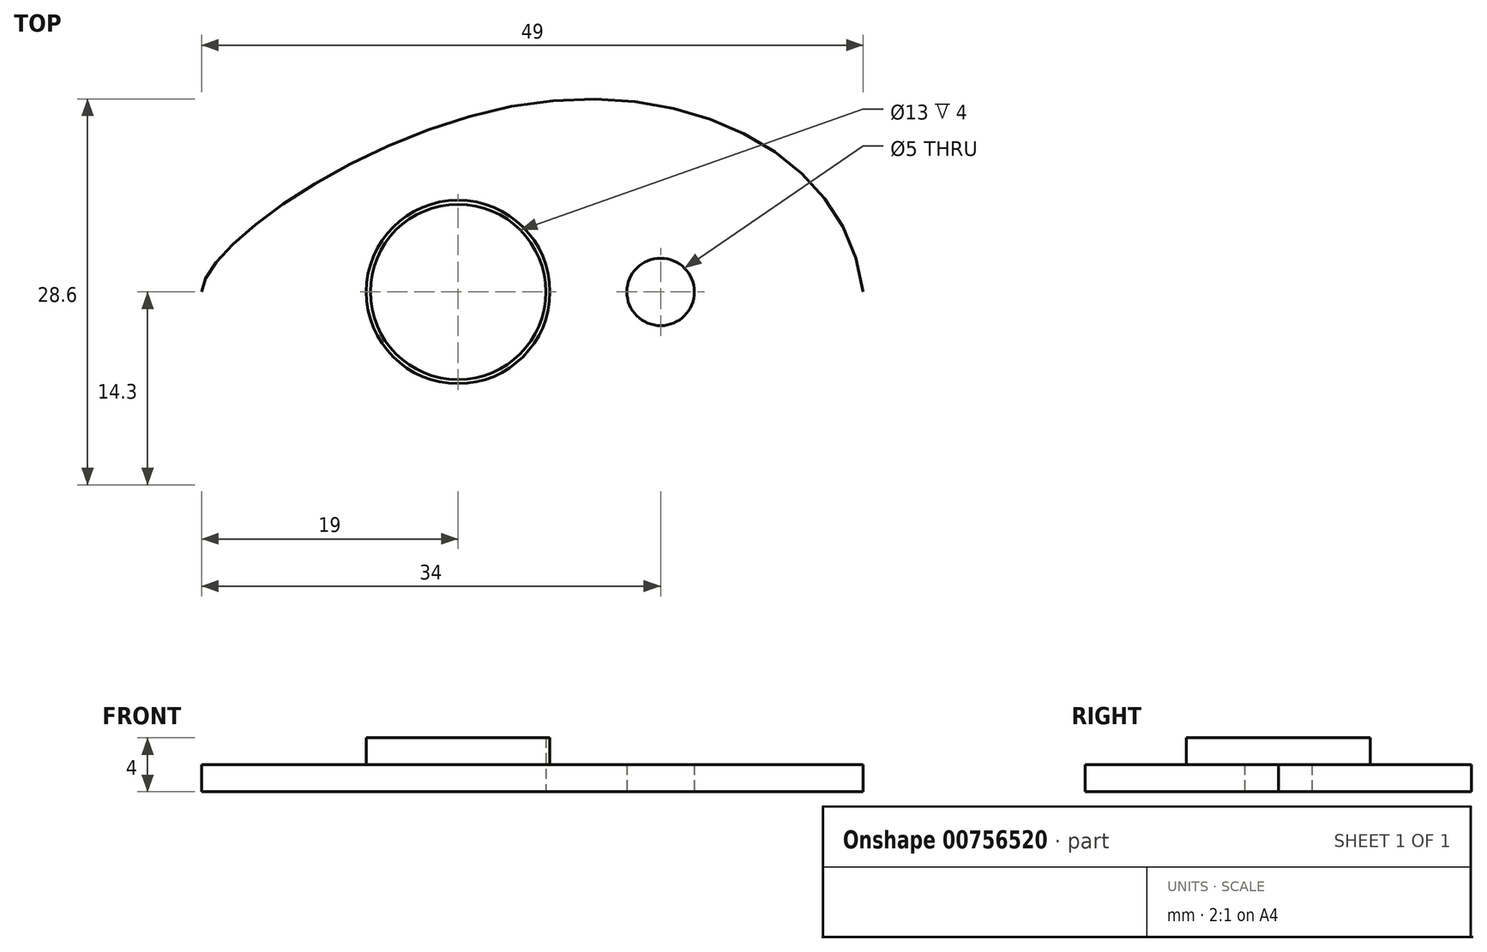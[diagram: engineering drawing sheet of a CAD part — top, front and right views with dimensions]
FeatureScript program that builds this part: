
annotation { "Feature Type Name" : "Feature", "Feature Type Description" : "" }
export const myFeature = defineFeature(function(context is Context, id is Id, definition is map)
    precondition{}
    {
        {
            var Q0;
            Q0=qCreatedBy(makeId("Top.planeOp"),FACE);
            var sketch = newSketch(context, id + "F0", { "sketchPlane" : qUnion([Q0])});
            skFitSpline(sketch, "E0", {"points": [v(-34, 0) * mm, v(-9.5, 14) * mm, v(15, 0) * mm], "startDerivative": vector(-0.01, 20.2) * mm, "endDerivative": vector(7.4, -60.56) * mm});
            skArc(sketch, "E1", {"start": v(-21.5, 0) * mm, "mid": v(-15, 6.5) * mm, "end": v(-8.5, 0) * mm});
            skPoint(sketch, "E1.startSnap0", {"position": v(-17, 0) * mm});
            skLineSegment(sketch, "E2", {"start": v(-34, 0) * mm, "end": v(-21.5, 0) * mm});
            skArc(sketch, "E3", {"start": v(-2.5, 0) * mm, "mid": v(0, 2.5) * mm, "end": v(2.5, 0) * mm});
            skLineSegment(sketch, "E4", {"start": v(-8.5, 0) * mm, "end": v(-2.5, 0) * mm});
            skLineSegment(sketch, "E5", {"start": v(2.5, 0) * mm, "end": v(15, 0) * mm});
            skSolve(sketch);
        }
        {
            var Q0;
            Q0=qSketchRegion(id+"F0",true);
            extrude(context, id + "F1", {"entities" : qUnion([Q0]), "depth" : 18 * mm, "offsetDistance" : 25 * mm});
        }
        {
            var Q0;
            Q0=makeQuery(id+"F1.opExtrude","SWEPT_BODY",BODY,{"disambiguationData":[OSD([sQuery(id+"F0.wireOp",EDGE,"E0"),sQuery(id+"F0.wireOp",EDGE,"E1"),sQuery(id+"F0.wireOp",EDGE,"McHGNHOU-62kw-HZgm-CWgZ-VDhnGf6BRuoS"),sQuery(id+"F0.wireOp",EDGE,"E2"),sQuery(id+"F0.wireOp",EDGE,"D958tiaN-heJL-5NL5-mns3-F5RS8ibdN3Pm"),sQuery(id+"F0.wireOp",EDGE,"xE7LKnkU-Hi0Y-gHIj-jbuS-JquG0hnZopf2")])]});
            var Q1;
            Q1=qCreatedBy(makeId("Front.planeOp"),FACE);
            mirror(context, id + "F2", {"operationType" : NewBodyOperationType.ADD, "entities" : qUnion([Q0]), "mirrorPlane" : qUnion([Q1])});
        }
        {
            var Q0;
            Q0=qCreatedBy(makeId("Top.planeOp"),FACE);
            var sketch = newSketch(context, id + "F3", { "sketchPlane" : qUnion([Q0])});
            skLineSegment(sketch, "E6", {"start": v(0, 0) * mm, "end": v(-15, 0) * mm});
            skCircle(sketch, "E7", {"center": v(-15, 0) * mm, "radius": 6.5 * mm});
            skCircle(sketch, "E8", {"center": v(-15, 0) * mm, "radius": 6.8 * mm});
            skSolve(sketch);
        }
        {
            var Q0;
            Q0=qSketchRegion(id+"F3",true);
            extrude(context, id + "F4", {"entities" : qUnion([Q0]), "operationType" : NewBodyOperationType.ADD, "depth" : 20 * mm, "offsetDistance" : 25 * mm});
        }
        {
            var Q0;
            Q0=qCreatedBy(makeId("Top.planeOp"),FACE);
            var sketch = newSketch(context, id + "F5", { "sketchPlane" : qUnion([Q0])});
            skCircle(sketch, "E9", {"center": v(0, 0) * mm, "radius": 4.75 * mm});
            skSolve(sketch);
        }
        {
            var Q0;
            Q0=qSketchRegion(id+"F5",true);
            extrude(context, id + "F6", {"entities" : qUnion([Q0]), "depth" : 15 * mm, "offsetDistance" : 25 * mm});
        }
        {
            var Q0;
            Q0=makeQuery(id+"F6.opExtrude","SWEPT_BODY",BODY,{"disambiguationData":[OSD([sQuery(id+"F5.wireOp",EDGE,"E9")])]});
            var Q1;
            Q1=makeQuery(id+"F1.opExtrude","SWEPT_BODY",BODY,{"disambiguationData":[OSD([sQuery(id+"F0.wireOp",EDGE,"E0"),sQuery(id+"F0.wireOp",EDGE,"E1"),sQuery(id+"F0.wireOp",EDGE,"McHGNHOU-62kw-HZgm-CWgZ-VDhnGf6BRuoS"),sQuery(id+"F0.wireOp",EDGE,"E2"),sQuery(id+"F0.wireOp",EDGE,"D958tiaN-heJL-5NL5-mns3-F5RS8ibdN3Pm"),sQuery(id+"F0.wireOp",EDGE,"xE7LKnkU-Hi0Y-gHIj-jbuS-JquG0hnZopf2")])]});
            booleanBodies(context, id + "F7", {"operationType" : BooleanOperationType.SUBTRACTION, "tools" : qUnion([Q0]), "targets" : qUnion([Q1])});
        }
        {
            var Q0;
            Q0=qCreatedBy(makeId("Top.planeOp"),FACE);
            var sketch = newSketch(context, id + "F8", { "sketchPlane" : qUnion([Q0])});
            skLineSegment(sketch, "E10.bottom", {"start": v(50, -30) * mm, "end": v(-50, -30) * mm});
            skLineSegment(sketch, "E10.top", {"start": v(50, 30) * mm, "end": v(-50, 30) * mm});
            skLineSegment(sketch, "E10.left", {"start": v(50, -30) * mm, "end": v(50, 30) * mm});
            skLineSegment(sketch, "E10.right", {"start": v(-50, -30) * mm, "end": v(-50, 30) * mm});
            skPoint(sketch, "E10.middle", {"position": v(0, 0) * mm});
            skSolve(sketch);
        }
        {
            var Q0;
            Q0=qSketchRegion(id+"F8",true);
            extrude(context, id + "F9", {"entities" : qUnion([Q0]), "depth" : 16 * mm, "offsetDistance" : 25 * mm});
        }
        {
            var Q0;
            Q0=makeQuery(id+"F9.opExtrude","SWEPT_BODY",BODY,{"disambiguationData":[OSD([sQuery(id+"F8.wireOp",EDGE,"E10.bottom"),sQuery(id+"F8.wireOp",EDGE,"E10.top"),sQuery(id+"F8.wireOp",EDGE,"E10.left"),sQuery(id+"F8.wireOp",EDGE,"E10.right")])]});
            var Q1;
            Q1=makeQuery(id+"F1.opExtrude","SWEPT_BODY",BODY,{"disambiguationData":[OSD([sQuery(id+"F0.wireOp",EDGE,"E0"),sQuery(id+"F0.wireOp",EDGE,"E1"),sQuery(id+"F0.wireOp",EDGE,"E2"),sQuery(id+"F0.wireOp",EDGE,"E3"),sQuery(id+"F0.wireOp",EDGE,"E4"),sQuery(id+"F0.wireOp",EDGE,"E5")])]});
            booleanBodies(context, id + "F10", {"operationType" : BooleanOperationType.SUBTRACTION, "tools" : qUnion([Q0]), "targets" : qUnion([Q1])});
        }
    });
